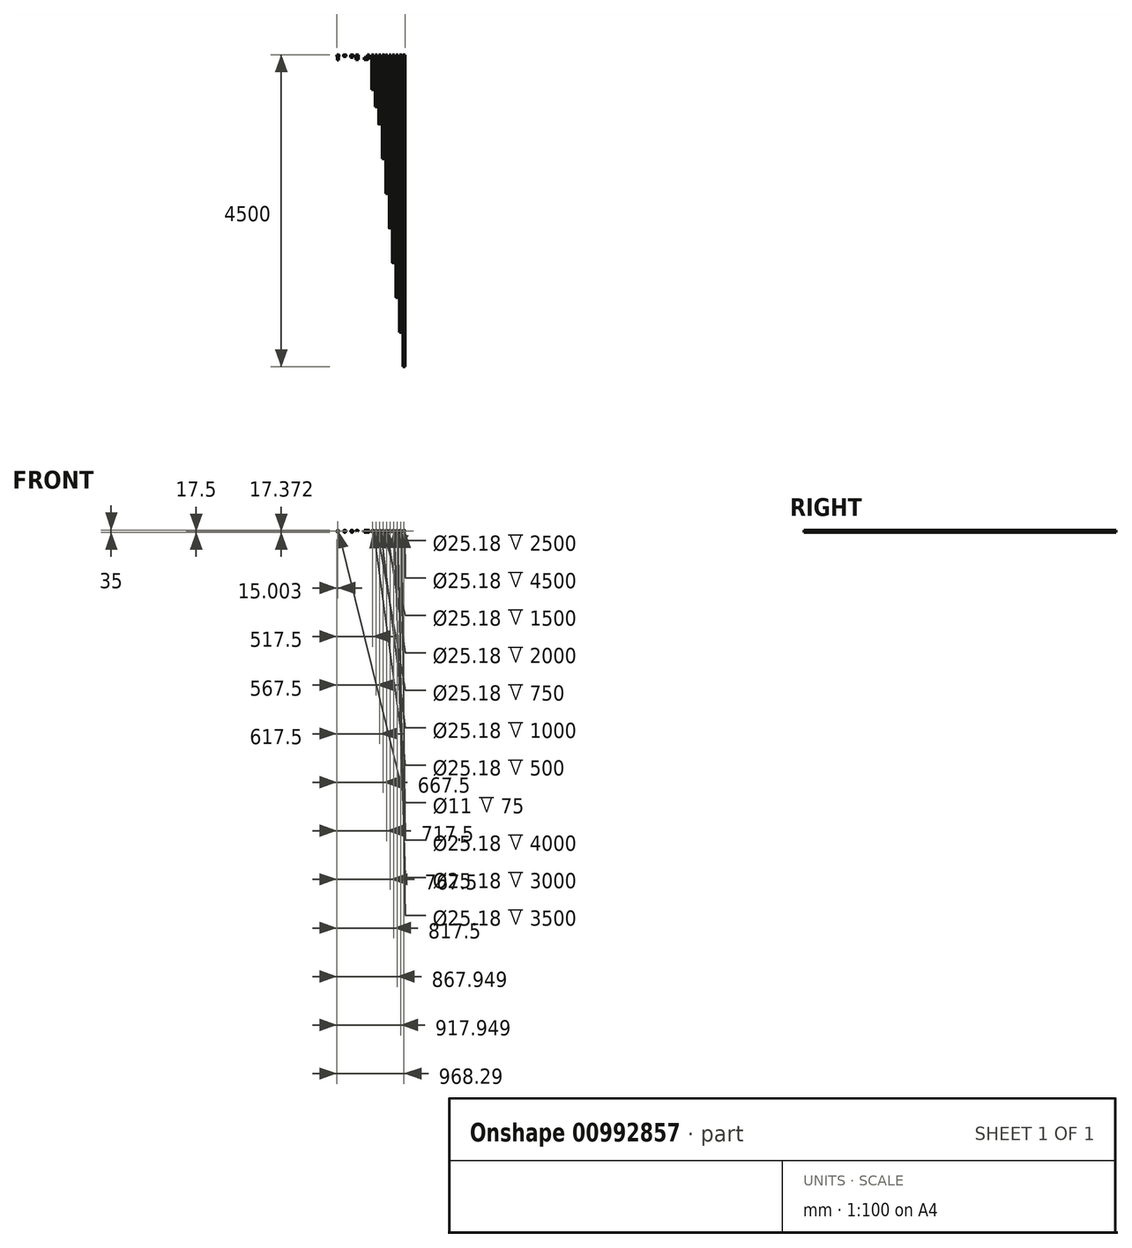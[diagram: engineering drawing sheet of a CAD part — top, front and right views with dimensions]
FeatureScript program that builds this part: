
annotation { "Feature Type Name" : "Feature", "Feature Type Description" : "" }
export const myFeature = defineFeature(function(context is Context, id is Id, definition is map)
    precondition{}
    {
        {
            var Q0;
            Q0=qCreatedBy(makeId("Front.planeOp"),FACE);
            var sketch = newSketch(context, id + "F0", { "sketchPlane" : qUnion([Q0])});
            skCircle(sketch, "E0", {"center": v(0, 0) * mm, "radius": 14.8 * mm});
            skCircle(sketch, "E1", {"center": v(0, 0) * mm, "radius": 12.59 * mm});
            skCircle(sketch, "E2", {"center": v(50, 0) * mm, "radius": 14.8 * mm});
            skCircle(sketch, "E3", {"center": v(50, 0) * mm, "radius": 12.59 * mm});
            skCircle(sketch, "E4", {"center": v(100, 0) * mm, "radius": 14.8 * mm});
            skCircle(sketch, "E5", {"center": v(100, 0) * mm, "radius": 12.59 * mm});
            skCircle(sketch, "E6", {"center": v(150, 0) * mm, "radius": 14.8 * mm});
            skCircle(sketch, "E7", {"center": v(150, 0) * mm, "radius": 12.59 * mm});
            skCircle(sketch, "E8", {"center": v(200, 0) * mm, "radius": 14.8 * mm});
            skCircle(sketch, "E9", {"center": v(200, 0) * mm, "radius": 12.59 * mm});
            skCircle(sketch, "E10", {"center": v(250, 0) * mm, "radius": 14.8 * mm});
            skCircle(sketch, "E11", {"center": v(250, 0) * mm, "radius": 12.59 * mm});
            skLineSegment(sketch, "E12", {"start": v(0, 0) * mm, "end": v(50, 0) * mm, "construction": true});
            skLineSegment(sketch, "E13", {"start": v(50, 0) * mm, "end": v(100, 0) * mm, "construction": true});
            skLineSegment(sketch, "E14", {"start": v(100, 0) * mm, "end": v(150, 0) * mm, "construction": true});
            skLineSegment(sketch, "E15", {"start": v(150, 0) * mm, "end": v(200, 0) * mm, "construction": true});
            skLineSegment(sketch, "E16", {"start": v(200, 0) * mm, "end": v(250, 0) * mm, "construction": true});
            skLineSegment(sketch, "E17", {"start": v(250, 0) * mm, "end": v(300, 0) * mm, "construction": true});
            skLineSegment(sketch, "E18", {"start": v(300, 0) * mm, "end": v(350.45, 0) * mm, "construction": true});
            skCircle(sketch, "E19", {"center": v(300, 0) * mm, "radius": 14.8 * mm});
            skCircle(sketch, "E20", {"center": v(300, 0) * mm, "radius": 12.59 * mm});
            skCircle(sketch, "E21", {"center": v(350.45, 0) * mm, "radius": 14.8 * mm});
            skCircle(sketch, "E22", {"center": v(350.45, 0) * mm, "radius": 12.59 * mm});
            skLineSegment(sketch, "E23", {"start": v(350.45, 0) * mm, "end": v(400.45, 0) * mm, "construction": true});
            skLineSegment(sketch, "E24", {"start": v(400.45, 0) * mm, "end": v(450.79, 0) * mm, "construction": true});
            skCircle(sketch, "E25", {"center": v(400.45, 0) * mm, "radius": 14.8 * mm});
            skCircle(sketch, "E26", {"center": v(400.45, 0) * mm, "radius": 12.59 * mm});
            skCircle(sketch, "E27", {"center": v(450.79, 0) * mm, "radius": 14.8 * mm});
            skCircle(sketch, "E28", {"center": v(450.79, 0) * mm, "radius": 12.59 * mm});
            skSolve(sketch);
        }
        {
            var Q0;
            Q0=makeQuery(id+"F0.imprint","IMPRINT",FACE,{"disambiguationData":[TD([[makeQuery(id+"F0.imprint","IMPRINT",EDGE,{"derivedFrom":sQuery(id+"F0.wireOp",EDGE,"E0")}),1.0]])]});
            extrude(context, id + "F1", {"entities" : qUnion([Q0]), "depth" : 500 * mm, "offsetDistance" : 25 * mm});
        }
        {
            var Q0;
            {var subQ0=sQuery(id+"F0.wireOp",EDGE,"E13");var subQ1=sQuery(id+"F0.wireOp",EDGE,"E2");var subQ2=makeQuery(id+"F0.imprint","INTERSECT",VERTEX,{"derivedFrom":[subQ1,subQ0]});Q0=makeQuery(id+"F0.imprint","IMPRINT",FACE,{"disambiguationData":[TD([[makeQuery(id+"F0.imprint","IMPRINT",EDGE,{"disambiguationData":[TD([[subQ2,1.0]])],"derivedFrom":subQ1}),1.0]])]});}
            var Q1;
            {var subQ0=sQuery(id+"F0.wireOp",EDGE,"E13");var subQ1=sQuery(id+"F0.wireOp",EDGE,"E2");var subQ2=makeQuery(id+"F0.imprint","INTERSECT",VERTEX,{"derivedFrom":[subQ1,subQ0]});Q1=makeQuery(id+"F0.imprint","IMPRINT",FACE,{"disambiguationData":[TD([[makeQuery(id+"F0.imprint","IMPRINT",EDGE,{"disambiguationData":[TD([[subQ2,-1.0]])],"derivedFrom":subQ1}),1.0]])]});}
            extrude(context, id + "F2", {"entities" : qUnion([Q0, Q1]), "depth" : 750 * mm, "offsetDistance" : 25 * mm});
        }
        {
            var Q0;
            {var subQ0=sQuery(id+"F0.wireOp",EDGE,"E14");var subQ1=sQuery(id+"F0.wireOp",EDGE,"E4");var subQ2=makeQuery(id+"F0.imprint","INTERSECT",VERTEX,{"derivedFrom":[subQ1,subQ0]});Q0=makeQuery(id+"F0.imprint","IMPRINT",FACE,{"disambiguationData":[TD([[makeQuery(id+"F0.imprint","IMPRINT",EDGE,{"disambiguationData":[TD([[subQ2,1.0]])],"derivedFrom":subQ1}),1.0]])]});}
            var Q1;
            {var subQ0=sQuery(id+"F0.wireOp",EDGE,"E14");var subQ1=sQuery(id+"F0.wireOp",EDGE,"E4");var subQ2=makeQuery(id+"F0.imprint","INTERSECT",VERTEX,{"derivedFrom":[subQ1,subQ0]});Q1=makeQuery(id+"F0.imprint","IMPRINT",FACE,{"disambiguationData":[TD([[makeQuery(id+"F0.imprint","IMPRINT",EDGE,{"disambiguationData":[TD([[subQ2,-1.0]])],"derivedFrom":subQ1}),1.0]])]});}
            extrude(context, id + "F3", {"entities" : qUnion([Q0, Q1]), "depth" : 1000 * mm, "offsetDistance" : 25 * mm});
        }
        {
            var Q0;
            {var subQ0=sQuery(id+"F0.wireOp",EDGE,"E15");var subQ1=sQuery(id+"F0.wireOp",EDGE,"E6");var subQ2=makeQuery(id+"F0.imprint","INTERSECT",VERTEX,{"derivedFrom":[subQ1,subQ0]});Q0=makeQuery(id+"F0.imprint","IMPRINT",FACE,{"disambiguationData":[TD([[makeQuery(id+"F0.imprint","IMPRINT",EDGE,{"disambiguationData":[TD([[subQ2,1.0]])],"derivedFrom":subQ1}),1.0]])]});}
            var Q1;
            {var subQ0=sQuery(id+"F0.wireOp",EDGE,"E15");var subQ1=sQuery(id+"F0.wireOp",EDGE,"E6");var subQ2=makeQuery(id+"F0.imprint","INTERSECT",VERTEX,{"derivedFrom":[subQ1,subQ0]});Q1=makeQuery(id+"F0.imprint","IMPRINT",FACE,{"disambiguationData":[TD([[makeQuery(id+"F0.imprint","IMPRINT",EDGE,{"disambiguationData":[TD([[subQ2,-1.0]])],"derivedFrom":subQ1}),1.0]])]});}
            extrude(context, id + "F4", {"entities" : qUnion([Q0, Q1]), "depth" : 1500 * mm, "offsetDistance" : 25 * mm});
        }
        {
            var Q0;
            {var subQ0=sQuery(id+"F0.wireOp",EDGE,"E16");var subQ1=sQuery(id+"F0.wireOp",EDGE,"E8");var subQ2=makeQuery(id+"F0.imprint","INTERSECT",VERTEX,{"derivedFrom":[subQ1,subQ0]});Q0=makeQuery(id+"F0.imprint","IMPRINT",FACE,{"disambiguationData":[TD([[makeQuery(id+"F0.imprint","IMPRINT",EDGE,{"disambiguationData":[TD([[subQ2,1.0]])],"derivedFrom":subQ1}),1.0]])]});}
            var Q1;
            {var subQ0=sQuery(id+"F0.wireOp",EDGE,"E16");var subQ1=sQuery(id+"F0.wireOp",EDGE,"E8");var subQ2=makeQuery(id+"F0.imprint","INTERSECT",VERTEX,{"derivedFrom":[subQ1,subQ0]});Q1=makeQuery(id+"F0.imprint","IMPRINT",FACE,{"disambiguationData":[TD([[makeQuery(id+"F0.imprint","IMPRINT",EDGE,{"disambiguationData":[TD([[subQ2,-1.0]])],"derivedFrom":subQ1}),1.0]])]});}
            extrude(context, id + "F5", {"entities" : qUnion([Q0, Q1]), "depth" : 2000 * mm, "offsetDistance" : 25 * mm});
        }
        {
            var Q0;
            {var subQ0=sQuery(id+"F0.wireOp",EDGE,"E17");var subQ1=sQuery(id+"F0.wireOp",EDGE,"E10");var subQ2=makeQuery(id+"F0.imprint","INTERSECT",VERTEX,{"derivedFrom":[subQ1,subQ0]});Q0=makeQuery(id+"F0.imprint","IMPRINT",FACE,{"disambiguationData":[TD([[makeQuery(id+"F0.imprint","IMPRINT",EDGE,{"disambiguationData":[TD([[subQ2,1.0]])],"derivedFrom":subQ1}),1.0]])]});}
            var Q1;
            {var subQ0=sQuery(id+"F0.wireOp",EDGE,"E17");var subQ1=sQuery(id+"F0.wireOp",EDGE,"E10");var subQ2=makeQuery(id+"F0.imprint","INTERSECT",VERTEX,{"derivedFrom":[subQ1,subQ0]});Q1=makeQuery(id+"F0.imprint","IMPRINT",FACE,{"disambiguationData":[TD([[makeQuery(id+"F0.imprint","IMPRINT",EDGE,{"disambiguationData":[TD([[subQ2,-1.0]])],"derivedFrom":subQ1}),1.0]])]});}
            extrude(context, id + "F6", {"entities" : qUnion([Q0, Q1]), "depth" : 2500 * mm, "offsetDistance" : 25 * mm});
        }
        {
            var Q0;
            {var subQ0=sQuery(id+"F0.wireOp",EDGE,"E27");var subQ1=makeQuery(id+"F0.imprint","IMPRINT",VERTEX,{"disambiguationData":[OD(0.0)],"derivedFrom":subQ0});Q0=makeQuery(id+"F0.imprint","IMPRINT",FACE,{"disambiguationData":[TD([[makeQuery(id+"F0.imprint","IMPRINT",EDGE,{"disambiguationData":[TD([[subQ1,1.0]])],"derivedFrom":subQ0}),1.0]])]});}
            extrude(context, id + "F7", {"entities" : qUnion([Q0]), "depth" : 4500 * mm, "offsetDistance" : 25 * mm});
        }
        {
            var Q0;
            Q0=makeQuery(id+"F0.imprint","IMPRINT",FACE,{"disambiguationData":[TD([[makeQuery(id+"F0.imprint","IMPRINT",EDGE,{"derivedFrom":sQuery(id+"F0.wireOp",EDGE,"E19")}),1.0]])]});
            extrude(context, id + "F8", {"entities" : qUnion([Q0]), "depth" : 3000 * mm, "offsetDistance" : 25 * mm});
        }
        {
            var Q0;
            Q0=makeQuery(id+"F0.imprint","IMPRINT",FACE,{"disambiguationData":[TD([[makeQuery(id+"F0.imprint","IMPRINT",EDGE,{"derivedFrom":sQuery(id+"F0.wireOp",EDGE,"E21")}),1.0]])]});
            extrude(context, id + "F9", {"entities" : qUnion([Q0]), "depth" : 3500 * mm, "offsetDistance" : 25 * mm});
        }
        {
            var Q0;
            Q0=makeQuery(id+"F0.imprint","IMPRINT",FACE,{"disambiguationData":[TD([[makeQuery(id+"F0.imprint","IMPRINT",EDGE,{"derivedFrom":sQuery(id+"F0.wireOp",EDGE,"E25")}),1.0]])]});
            extrude(context, id + "F10", {"entities" : qUnion([Q0]), "depth" : 4000 * mm, "offsetDistance" : 25 * mm});
        }
        {
            var Q0;
            Q0=qCreatedBy(makeId("Front.planeOp"),FACE);
            var sketch = newSketch(context, id + "F11", { "sketchPlane" : qUnion([Q0])});
            skCircle(sketch, "E29", {"center": v(-63.01, 0) * mm, "radius": 15 * mm});
            skCircle(sketch, "E30", {"center": v(-63.01, 0) * mm, "radius": 17.5 * mm});
            skSolve(sketch);
        }
        {
            var Q0;
            Q0=qCreatedBy(makeId("Top.planeOp"),FACE);
            var sketch = newSketch(context, id + "F12", { "sketchPlane" : qUnion([Q0])});
            skPoint(sketch, "E31", {"position": v(-63, 0) * mm});
            skLineSegment(sketch, "E32.left", {"start": v(-63, 0) * mm, "end": v(-63, -25) * mm});
            skPoint(sketch, "E33", {"position": v(-62.99, 0) * mm});
            skArc(sketch, "E34", {"start": v(-93, -55) * mm, "mid": v(-71.78, -46.21) * mm, "end": v(-63, -25) * mm});
            skLineSegment(sketch, "E35", {"start": v(-93, -55) * mm, "end": v(-122.82, -55) * mm});
            skSolve(sketch);
        }
        {
            var Q0;
            Q0=makeQuery(id+"F11.imprint","IMPRINT",FACE,{"disambiguationData":[TD([[makeQuery(id+"F11.imprint","IMPRINT",EDGE,{"derivedFrom":sQuery(id+"F11.wireOp",EDGE,"E29")}),-1.0]])]});
            var Q1;
            Q1=sQuery(id+"F12.wireOp",EDGE,"E32.left");
            var Q2;
            Q2=sQuery(id+"F12.wireOp",EDGE,"E34");
            var Q3;
            Q3=sQuery(id+"F12.wireOp",EDGE,"E35");
            sweep(context, id + "F13", {"profiles" : qUnion([Q0]), "path" : qUnion([Q1, Q2, Q3])});
        }
        {
            var Q0;
            Q0=qCreatedBy(makeId("Front.planeOp"),FACE);
            var sketch = newSketch(context, id + "F14", { "sketchPlane" : qUnion([Q0])});
            skLineSegment(sketch, "E36", {"start": v(0, 0) * mm, "end": v(-300, 0) * mm});
            skCircle(sketch, "E37", {"center": v(-300, 0) * mm, "radius": 17.5 * mm});
            skCircle(sketch, "E38", {"center": v(-300, 0) * mm, "radius": 15 * mm});
            skCircle(sketch, "E39", {"center": v(-224.78, -0.13) * mm, "radius": 17.5 * mm});
            skCircle(sketch, "E40", {"center": v(-224.78, -0.13) * mm, "radius": 15 * mm});
            skCircle(sketch, "E41", {"center": v(-402.76, 0) * mm, "radius": 17.5 * mm});
            skCircle(sketch, "E42", {"center": v(-402.76, 0) * mm, "radius": 15 * mm});
            skCircle(sketch, "E43", {"center": v(-502.5, -0.13) * mm, "radius": 15 * mm});
            skCircle(sketch, "E44", {"center": v(-502.5, -0.13) * mm, "radius": 7.5 * mm});
            skCircle(sketch, "E45", {"center": v(-502.5, -0.13) * mm, "radius": 5.5 * mm});
            skSolve(sketch);
        }
        {
            var Q0;
            Q0=makeQuery(id+"F14.imprint","IMPRINT",FACE,{"disambiguationData":[TD([[makeQuery(id+"F14.imprint","IMPRINT",EDGE,{"derivedFrom":sQuery(id+"F14.wireOp",EDGE,"E37")}),1.0]])]});
            extrude(context, id + "F15", {"entities" : qUnion([Q0]), "depth" : 37.5 * mm, "offsetDistance" : 25 * mm});
        }
        {
            var Q0;
            {var subQ0=sQuery(id+"F14.wireOp",EDGE,"E39");var subQ1=sQuery(id+"F14.wireOp",EDGE,"E36");var subQ2=makeQuery(id+"F14.imprint","INTERSECT",VERTEX,{"disambiguationData":[OD(0.0)],"derivedFrom":[subQ1,subQ0]});Q0=makeQuery(id+"F14.imprint","IMPRINT",FACE,{"disambiguationData":[TD([[makeQuery(id+"F14.imprint","IMPRINT",EDGE,{"disambiguationData":[TD([[subQ2,1.0]])],"derivedFrom":subQ1}),-1.0]])]});}
            var Q1;
            {var subQ0=sQuery(id+"F14.wireOp",EDGE,"E40");var subQ1=makeQuery(id+"F14.imprint","IMPRINT",VERTEX,{"derivedFrom":subQ0});Q1=makeQuery(id+"F14.imprint","IMPRINT",FACE,{"disambiguationData":[TD([[makeQuery(id+"F14.imprint","IMPRINT",EDGE,{"disambiguationData":[TD([[subQ1,-1.0]])],"derivedFrom":subQ0}),-1.0]])]});}
            extrude(context, id + "F16", {"entities" : qUnion([Q0, Q1]), "depth" : 70 * mm, "offsetDistance" : 25 * mm});
        }
        {
            var Q0;
            Q0=makeQuery(id+"F14.imprint","IMPRINT",FACE,{"disambiguationData":[TD([[makeQuery(id+"F14.imprint","IMPRINT",EDGE,{"derivedFrom":sQuery(id+"F14.wireOp",EDGE,"E42")}),1.0]])]});
            extrude(context, id + "F17", {"entities" : qUnion([Q0]), "depth" : 5 * mm, "offsetDistance" : 25 * mm});
        }
        {
            var Q0;
            Q0=makeQuery(id+"F14.imprint","IMPRINT",FACE,{"disambiguationData":[TD([[makeQuery(id+"F14.imprint","IMPRINT",EDGE,{"derivedFrom":sQuery(id+"F14.wireOp",EDGE,"E41")}),1.0]])]});
            extrude(context, id + "F18", {"entities" : qUnion([Q0]), "operationType" : NewBodyOperationType.ADD, "depth" : 25 * mm, "offsetDistance" : 25 * mm});
        }
        {
            var Q0;
            Q0=makeQuery(id+"F18.opExtrude","CAP_EDGE",EDGE,{"disambiguationData":[OSD([sQuery(id+"F14.wireOp",EDGE,"E41")])],"isStart":true});
            fillet(context, id + "F19", {"entities" : qUnion([Q0]), "tangentPropagation" : true, "radius" : 5 * mm, "defaultsChanged" : false, "vertexSettings" : [], "allowEdgeOverflow" : false});
        }
        {
            var Q0;
            Q0=makeQuery(id+"F18.opExtrude","CAP_EDGE",EDGE,{"disambiguationData":[OSD([sQuery(id+"F14.wireOp",EDGE,"E41")])],"isStart":false});
            chamfer(context, id + "F20", {"entities" : qUnion([Q0]), "width" : 1 * mm, "tangentPropagation" : true});
        }
        {
            var Q0;
            Q0=makeQuery(id+"F14.imprint","IMPRINT",FACE,{"disambiguationData":[TD([[makeQuery(id+"F14.imprint","IMPRINT",EDGE,{"derivedFrom":sQuery(id+"F14.wireOp",EDGE,"E43")}),1.0]])]});
            extrude(context, id + "F21", {"entities" : qUnion([Q0]), "depth" : 25 * mm, "offsetDistance" : 25 * mm});
        }
        {
            var Q0;
            Q0=makeQuery(id+"F14.imprint","IMPRINT",FACE,{"disambiguationData":[TD([[makeQuery(id+"F14.imprint","IMPRINT",EDGE,{"derivedFrom":sQuery(id+"F14.wireOp",EDGE,"E44")}),1.0]])]});
            extrude(context, id + "F22", {"entities" : qUnion([Q0]), "operationType" : NewBodyOperationType.ADD, "depth" : 75 * mm, "offsetDistance" : 25 * mm});
        }
    });
